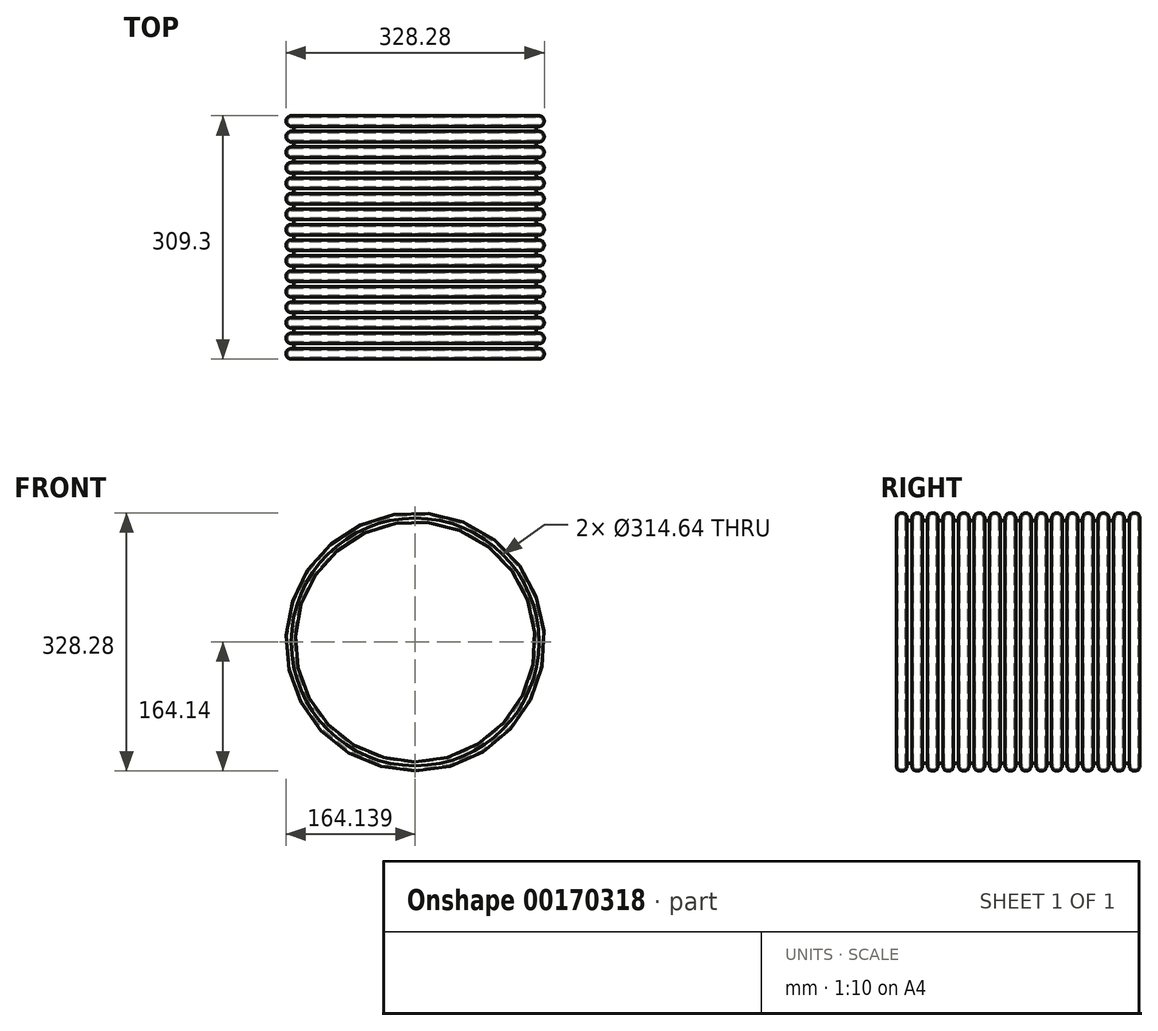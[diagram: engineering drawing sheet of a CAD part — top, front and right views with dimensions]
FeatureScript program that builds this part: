
annotation { "Feature Type Name" : "Feature", "Feature Type Description" : "" }
export const myFeature = defineFeature(function(context is Context, id is Id, definition is map)
    precondition{}
    {
        {
            var Q0;
            Q0=qCreatedBy(makeId("Top.planeOp"),FACE);
            var sketch = newSketch(context, id + "F0", { "sketchPlane" : qUnion([Q0])});
            skArc(sketch, "E0", {"start": v(0, 0) * mm, "mid": v(4.92, 4.92) * mm, "end": v(0, 9.84) * mm});
            skLineSegment(sketch, "E1", {"start": v(0, 0) * mm, "end": v(0, 307.4) * mm, "construction": true});
            skArc(sketch, "E2.0.1.0", {"start": v(0, 19.71) * mm, "mid": v(4.92, 24.63) * mm, "end": v(0, 29.55) * mm});
            skArc(sketch, "E2.0.2.0", {"start": v(0, 39.42) * mm, "mid": v(4.92, 44.34) * mm, "end": v(0, 49.26) * mm});
            skArc(sketch, "E2.0.3.0", {"start": v(0, 59.13) * mm, "mid": v(4.92, 64.05) * mm, "end": v(0, 68.97) * mm});
            skArc(sketch, "E2.0.4.0", {"start": v(0, 78.84) * mm, "mid": v(4.92, 83.76) * mm, "end": v(0, 88.68) * mm});
            skArc(sketch, "E2.0.5.0", {"start": v(0, 98.55) * mm, "mid": v(4.92, 103.47) * mm, "end": v(0, 108.4) * mm});
            skArc(sketch, "E2.0.6.0", {"start": v(0, 118.26) * mm, "mid": v(4.92, 123.18) * mm, "end": v(0, 128.1) * mm});
            skArc(sketch, "E2.0.7.0", {"start": v(0, 137.97) * mm, "mid": v(4.92, 142.9) * mm, "end": v(0, 147.82) * mm});
            skArc(sketch, "E2.0.8.0", {"start": v(0, 157.68) * mm, "mid": v(4.92, 162.6) * mm, "end": v(0, 167.53) * mm});
            skArc(sketch, "E2.0.9.0", {"start": v(0, 177.4) * mm, "mid": v(4.92, 182.31) * mm, "end": v(0, 187.24) * mm});
            skArc(sketch, "E2.0.10.0", {"start": v(0, 197.1) * mm, "mid": v(4.92, 202.03) * mm, "end": v(0, 206.95) * mm});
            skArc(sketch, "E2.0.11.0", {"start": v(0, 216.81) * mm, "mid": v(4.92, 221.74) * mm, "end": v(0, 226.66) * mm});
            skLineSegment(sketch, "E2.direction2", {"start": v(0, 0) * mm, "end": v(0, 19.71) * mm, "construction": true});
            skArc(sketch, "E3.0.0.12", {"start": v(0, 236.52) * mm, "mid": v(4.92, 241.45) * mm, "end": v(0, 246.37) * mm});
            skArc(sketch, "E3.0.0.13", {"start": v(0, 256.24) * mm, "mid": v(4.92, 261.16) * mm, "end": v(0, 266.08) * mm});
            skArc(sketch, "E3.0.0.14", {"start": v(0, 275.95) * mm, "mid": v(4.92, 280.87) * mm, "end": v(0, 285.79) * mm});
            skArc(sketch, "E4.0.0.15", {"start": v(0, 295.66) * mm, "mid": v(4.92, 300.58) * mm, "end": v(0, 305.5) * mm});
            skArc(sketch, "E5", {"start": v(0, 19.71) * mm, "mid": v(-4.93, 14.78) * mm, "end": v(0, 9.84) * mm});
            skArc(sketch, "E6.0.1.0", {"start": v(0, 39.42) * mm, "mid": v(-4.93, 34.49) * mm, "end": v(0, 29.55) * mm});
            skArc(sketch, "E6.0.2.0", {"start": v(0, 59.13) * mm, "mid": v(-4.93, 54.2) * mm, "end": v(0, 49.26) * mm});
            skArc(sketch, "E6.0.3.0", {"start": v(0, 78.84) * mm, "mid": v(-4.93, 73.9) * mm, "end": v(0, 68.97) * mm});
            skArc(sketch, "E6.0.4.0", {"start": v(0, 98.55) * mm, "mid": v(-4.93, 93.62) * mm, "end": v(0, 88.68) * mm});
            skArc(sketch, "E6.0.5.0", {"start": v(0, 118.26) * mm, "mid": v(-4.93, 113.33) * mm, "end": v(0, 108.4) * mm});
            skArc(sketch, "E6.0.6.0", {"start": v(0, 137.97) * mm, "mid": v(-4.93, 133.04) * mm, "end": v(0, 128.1) * mm});
            skArc(sketch, "E6.0.7.0", {"start": v(0, 157.68) * mm, "mid": v(-4.93, 152.75) * mm, "end": v(0, 147.82) * mm});
            skArc(sketch, "E6.0.8.0", {"start": v(0, 177.4) * mm, "mid": v(-4.93, 172.46) * mm, "end": v(0, 167.53) * mm});
            skArc(sketch, "E6.0.9.0", {"start": v(0, 197.1) * mm, "mid": v(-4.93, 192.17) * mm, "end": v(0, 187.24) * mm});
            skArc(sketch, "E6.0.10.0", {"start": v(0, 216.81) * mm, "mid": v(-4.93, 211.88) * mm, "end": v(0, 206.95) * mm});
            skArc(sketch, "E6.0.11.0", {"start": v(0, 236.52) * mm, "mid": v(-4.93, 231.6) * mm, "end": v(0, 226.66) * mm});
            skArc(sketch, "E6.0.12.0", {"start": v(0, 256.24) * mm, "mid": v(-4.93, 251.3) * mm, "end": v(0, 246.37) * mm});
            skArc(sketch, "E6.0.13.0", {"start": v(0, 275.95) * mm, "mid": v(-4.93, 271.01) * mm, "end": v(0, 266.08) * mm});
            skArc(sketch, "E6.0.14.0", {"start": v(0, 295.66) * mm, "mid": v(-4.93, 290.72) * mm, "end": v(0, 285.79) * mm});
            skArc(sketch, "E7.0", {"start": v(0, -1.9) * mm, "mid": v(6.82, 4.92) * mm, "end": v(0, 11.74) * mm});
            skArc(sketch, "E8.0", {"start": v(0, 17.81) * mm, "mid": v(-3.04, 14.78) * mm, "end": v(0, 11.74) * mm});
            skArc(sketch, "E9.0", {"start": v(0, 17.81) * mm, "mid": v(6.82, 24.63) * mm, "end": v(0, 31.45) * mm});
            skArc(sketch, "E10.0.1.0", {"start": v(0, 37.52) * mm, "mid": v(-3.04, 34.49) * mm, "end": v(0, 31.45) * mm});
            skArc(sketch, "E10.0.1.1", {"start": v(0, 37.52) * mm, "mid": v(6.82, 44.34) * mm, "end": v(0, 51.16) * mm});
            skArc(sketch, "E10.0.2.0", {"start": v(0, 57.23) * mm, "mid": v(-3.04, 54.2) * mm, "end": v(0, 51.16) * mm});
            skArc(sketch, "E10.0.2.1", {"start": v(0, 57.23) * mm, "mid": v(6.82, 64.05) * mm, "end": v(0, 70.87) * mm});
            skArc(sketch, "E10.0.3.0", {"start": v(0, 76.94) * mm, "mid": v(-3.04, 73.9) * mm, "end": v(0, 70.87) * mm});
            skArc(sketch, "E10.0.3.1", {"start": v(0, 76.94) * mm, "mid": v(6.82, 83.76) * mm, "end": v(0, 90.58) * mm});
            skArc(sketch, "E10.0.4.0", {"start": v(0, 96.65) * mm, "mid": v(-3.04, 93.62) * mm, "end": v(0, 90.58) * mm});
            skArc(sketch, "E10.0.4.1", {"start": v(0, 96.65) * mm, "mid": v(6.82, 103.47) * mm, "end": v(0, 110.3) * mm});
            skArc(sketch, "E10.0.5.0", {"start": v(0, 116.37) * mm, "mid": v(-3.04, 113.33) * mm, "end": v(0, 110.3) * mm});
            skArc(sketch, "E10.0.5.1", {"start": v(0, 116.37) * mm, "mid": v(6.82, 123.18) * mm, "end": v(0, 130) * mm});
            skArc(sketch, "E10.0.6.0", {"start": v(0, 136.08) * mm, "mid": v(-3.04, 133.04) * mm, "end": v(0, 130) * mm});
            skArc(sketch, "E10.0.6.1", {"start": v(0, 136.08) * mm, "mid": v(6.82, 142.9) * mm, "end": v(0, 149.71) * mm});
            skArc(sketch, "E10.0.7.0", {"start": v(0, 155.79) * mm, "mid": v(-3.04, 152.75) * mm, "end": v(0, 149.71) * mm});
            skArc(sketch, "E10.0.7.1", {"start": v(0, 155.79) * mm, "mid": v(6.82, 162.6) * mm, "end": v(0, 169.42) * mm});
            skArc(sketch, "E10.0.8.0", {"start": v(0, 175.5) * mm, "mid": v(-3.04, 172.46) * mm, "end": v(0, 169.42) * mm});
            skArc(sketch, "E10.0.8.1", {"start": v(0, 175.5) * mm, "mid": v(6.82, 182.31) * mm, "end": v(0, 189.13) * mm});
            skArc(sketch, "E10.0.9.0", {"start": v(0, 195.2) * mm, "mid": v(-3.04, 192.17) * mm, "end": v(0, 189.13) * mm});
            skArc(sketch, "E10.0.9.1", {"start": v(0, 195.2) * mm, "mid": v(6.82, 202.03) * mm, "end": v(0, 208.84) * mm});
            skArc(sketch, "E10.0.10.0", {"start": v(0, 214.92) * mm, "mid": v(-3.04, 211.88) * mm, "end": v(0, 208.84) * mm});
            skArc(sketch, "E10.0.10.1", {"start": v(0, 214.92) * mm, "mid": v(6.82, 221.74) * mm, "end": v(0, 228.55) * mm});
            skArc(sketch, "E10.0.11.0", {"start": v(0, 234.63) * mm, "mid": v(-3.04, 231.6) * mm, "end": v(0, 228.55) * mm});
            skArc(sketch, "E10.0.11.1", {"start": v(0, 234.63) * mm, "mid": v(6.82, 241.45) * mm, "end": v(0, 248.26) * mm});
            skArc(sketch, "E10.0.12.0", {"start": v(0, 254.34) * mm, "mid": v(-3.04, 251.3) * mm, "end": v(0, 248.26) * mm});
            skArc(sketch, "E10.0.12.1", {"start": v(0, 254.34) * mm, "mid": v(6.82, 261.16) * mm, "end": v(0, 267.98) * mm});
            skArc(sketch, "E10.0.13.0", {"start": v(0, 274.05) * mm, "mid": v(-3.04, 271.01) * mm, "end": v(0, 267.98) * mm});
            skArc(sketch, "E10.0.13.1", {"start": v(0, 274.05) * mm, "mid": v(6.82, 280.87) * mm, "end": v(0, 287.69) * mm});
            skArc(sketch, "E10.0.14.0", {"start": v(0, 293.76) * mm, "mid": v(-3.04, 290.72) * mm, "end": v(0, 287.69) * mm});
            skArc(sketch, "E10.0.14.1", {"start": v(0, 293.76) * mm, "mid": v(6.82, 300.58) * mm, "end": v(0, 307.4) * mm});
            skLineSegment(sketch, "E11", {"start": v(0, 307.4) * mm, "end": v(0, 305.5) * mm});
            skLineSegment(sketch, "E12", {"start": v(0, -1.9) * mm, "end": v(0, 0) * mm});
            skSolve(sketch);
        }
        {
            var Q0;
            Q0=qCreatedBy(makeId("Top.planeOp"),FACE);
            var sketch = newSketch(context, id + "F1", { "sketchPlane" : qUnion([Q0])});
            skLineSegment(sketch, "E13", {"start": v(-157.32, 0) * mm, "end": v(-157.32, 304.8) * mm, "construction": true});
            skSolve(sketch);
        }
        {
            var Q0;
            Q0 = qSketchRegion(id + "F0", true);
            var Q1;
            Q1=sQuery(id+"F1.wireOp",EDGE,"E13");
            revolve(context, id + "F2", {"entities" : qUnion([Q0]), "axis" : qUnion([Q1]), "revolveType" : RevolveType.FULL});
        }
    });
